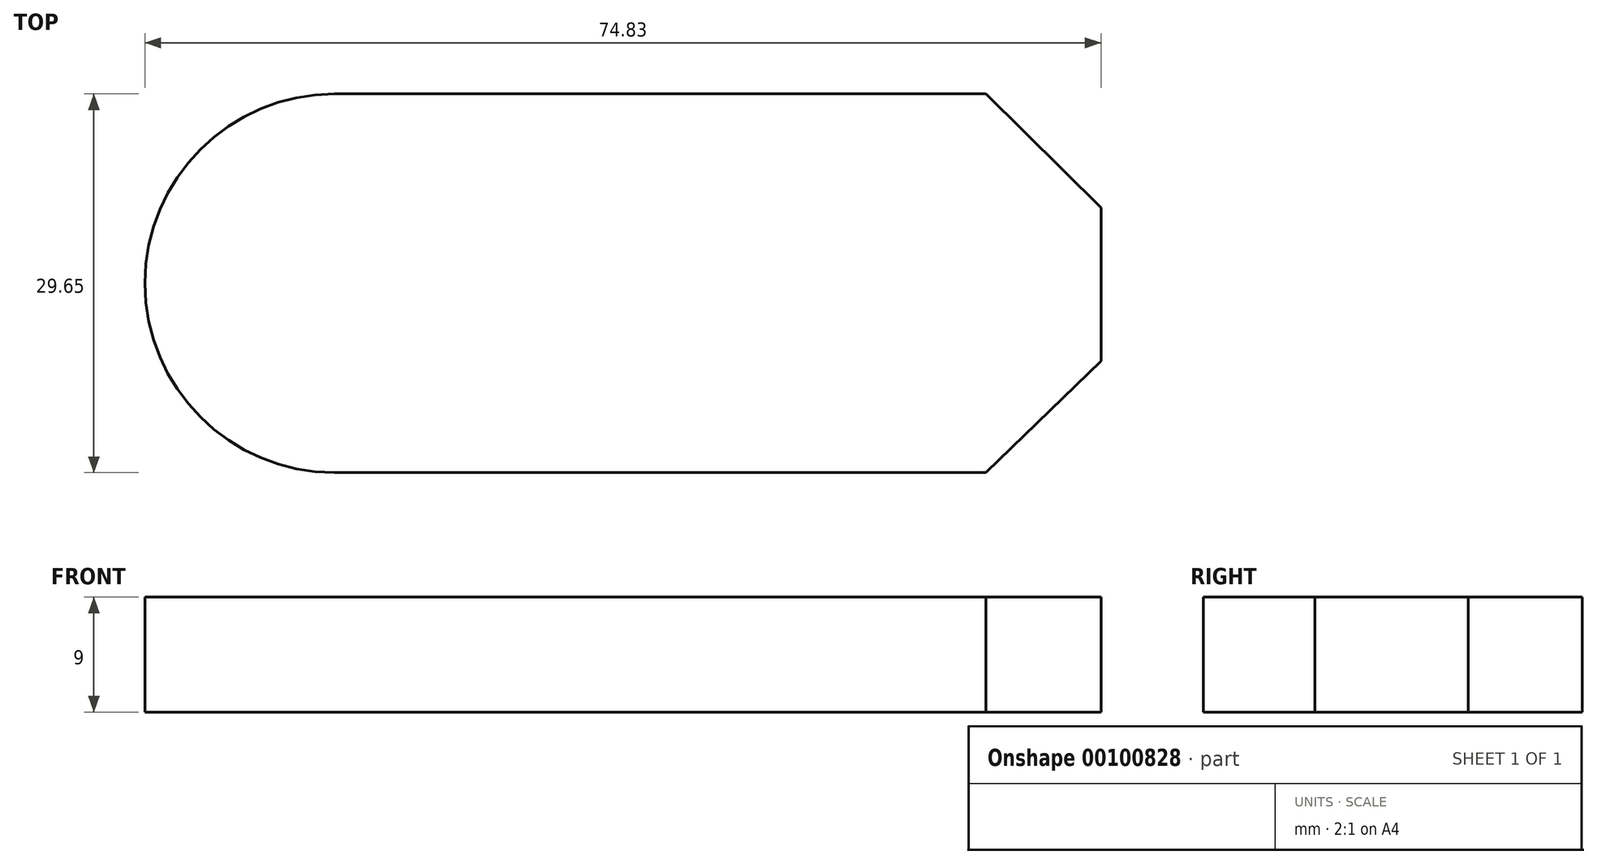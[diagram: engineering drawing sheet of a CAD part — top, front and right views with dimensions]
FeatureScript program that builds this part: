
annotation { "Feature Type Name" : "Feature", "Feature Type Description" : "" }
export const myFeature = defineFeature(function(context is Context, id is Id, definition is map)
    precondition{}
    {
        {
            var Q0;
            Q0=qCreatedBy(makeId("Top.planeOp"),FACE);
            var sketch = newSketch(context, id + "F0", { "sketchPlane" : qUnion([Q0])});
            skLineSegment(sketch, "E0.bottom", {"start": v(0, 0) * mm, "end": v(51, 0) * mm});
            skLineSegment(sketch, "E0.top", {"start": v(0, 29.65) * mm, "end": v(51, 29.65) * mm});
            skLineSegment(sketch, "E0.left", {"start": v(0, 0) * mm, "end": v(0, 29.65) * mm});
            skArc(sketch, "E1", {"start": v(0, 29.65) * mm, "mid": v(-14.83, 14.83) * mm, "end": v(0, 0) * mm});
            skLineSegment(sketch, "E2", {"start": v(60, 20.73) * mm, "end": v(60, 8.73) * mm});
            skLineSegment(sketch, "E3", {"start": v(51, 0) * mm, "end": v(60, 8.73) * mm});
            skLineSegment(sketch, "E4", {"start": v(51, 29.65) * mm, "end": v(60, 20.73) * mm});
            skLineSegment(sketch, "E5", {"start": v(0, 0) * mm, "end": v(18, 0) * mm});
            skLineSegment(sketch, "E6", {"start": v(18, 0) * mm, "end": v(18, 29.65) * mm});
            skSolve(sketch);
        }
        {
            var Q0;
            Q0 = qSketchRegion(id + "FM5KE1gofh7Nzut_0", true);
            var Q1;
            Q1 = qSketchRegion(id + "F0", true);
            extrude(context, id + "F1", {"entities" : qUnion([Q0, Q1]), "depth" : 9 * mm});
        }
    });
